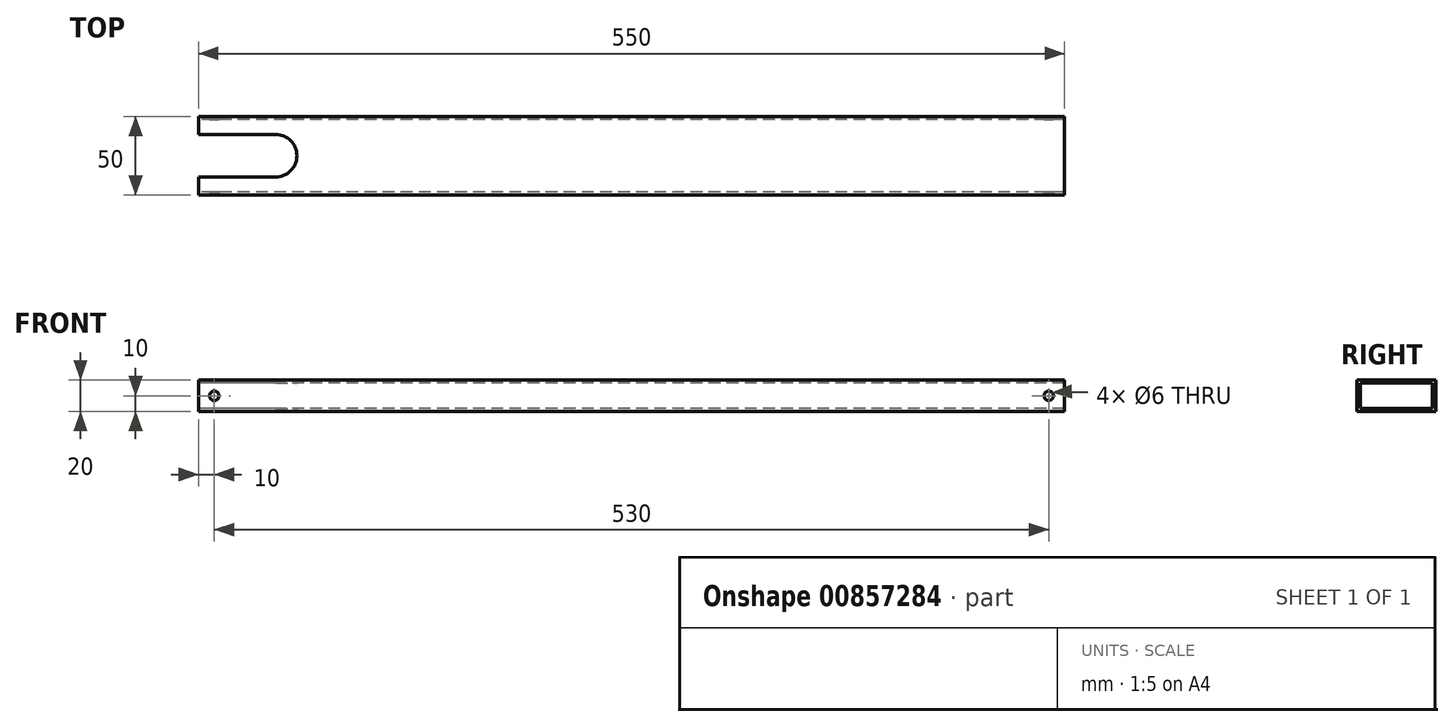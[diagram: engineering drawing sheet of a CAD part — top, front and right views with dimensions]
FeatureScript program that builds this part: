
annotation { "Feature Type Name" : "Feature", "Feature Type Description" : "" }
export const myFeature = defineFeature(function(context is Context, id is Id, definition is map)
    precondition{}
    {
        {
            var Q0;
            Q0=qCreatedBy(makeId("Right.planeOp"),FACE);
            var sketch = newSketch(context, id + "F0", { "sketchPlane" : qUnion([Q0])});
            skLineSegment(sketch, "E0.bottom", {"start": v(0, 0) * mm, "end": v(50, 0) * mm});
            skLineSegment(sketch, "E0.top", {"start": v(0, 20) * mm, "end": v(50, 20) * mm});
            skLineSegment(sketch, "E0.left", {"start": v(0, 0) * mm, "end": v(0, 20) * mm});
            skLineSegment(sketch, "E0.right", {"start": v(50, 0) * mm, "end": v(50, 20) * mm});
            skLineSegment(sketch, "E1.0", {"start": v(2, 18) * mm, "end": v(48, 18) * mm});
            skLineSegment(sketch, "E1.1", {"start": v(2, 2) * mm, "end": v(2, 18) * mm});
            skLineSegment(sketch, "E1.2", {"start": v(2, 2) * mm, "end": v(48, 2) * mm});
            skLineSegment(sketch, "E1.3", {"start": v(48, 2) * mm, "end": v(48, 18) * mm});
            skSolve(sketch);
        }
        {
            var Q0;
            Q0=makeQuery(id+"F0.imprint","IMPRINT",FACE,{"disambiguationData":[TD([[makeQuery(id+"F0.imprint","IMPRINT",EDGE,{"derivedFrom":sQuery(id+"F0.wireOp",EDGE,"E0.bottom")}),1.0]])]});
            extrude(context, id + "F1", {"entities" : qUnion([Q0]), "depth" : 550 * mm, "offsetDistance" : 25.4 * mm});
        }
        {
            var Q0;
            Q0=makeQuery(id+"F1.opExtrude","SWEPT_FACE",FACE,{"disambiguationData":[OSD([sQuery(id+"F0.wireOp",EDGE,"E0.left")])]});
            var sketch = newSketch(context, id + "F2", { "sketchPlane" : qUnion([Q0])});
            skCircle(sketch, "E2", {"center": v(10, 10) * mm, "radius": 3 * mm});
            skCircle(sketch, "E3", {"center": v(540, 10) * mm, "radius": 3 * mm});
            skPoint(sketch, "E3.centerSnap0", {"position": v(550, 10) * mm});
            skLineSegment(sketch, "E4", {"start": v(0, 10) * mm, "end": v(550, 10) * mm, "construction": true});
            skSolve(sketch);
        }
        {
            var Q0;
            Q0 = qSketchRegion(id + "F2", true);
            extrude(context, id + "F3", {"entities" : qUnion([Q0]), "operationType" : NewBodyOperationType.REMOVE, "endBound" : BoundingType.THROUGH_ALL, "oppositeDirection" : true, "depth" : 25.4 * mm, "offsetDistance" : 25.4 * mm});
        }
        {
            var Q0;
            Q0=makeQuery(id+"F1.opExtrude","SWEPT_FACE",FACE,{"disambiguationData":[OSD([sQuery(id+"F0.wireOp",EDGE,"E0.top")])]});
            var sketch = newSketch(context, id + "F4", { "sketchPlane" : qUnion([Q0])});
            skLineSegment(sketch, "E5", {"start": v(10, 0) * mm, "end": v(10, 50) * mm, "construction": true});
            skArc(sketch, "E6", {"start": v(49, 11.5) * mm, "mid": v(62.5, 25) * mm, "end": v(49, 38.5) * mm});
            skLineSegment(sketch, "E7", {"start": v(0, 25) * mm, "end": v(125, 25) * mm, "construction": true});
            skLineSegment(sketch, "E8", {"start": v(49, 38.5) * mm, "end": v(0, 38.5) * mm});
            skLineSegment(sketch, "E9", {"start": v(49, 11.5) * mm, "end": v(0, 11.5) * mm});
            skLineSegment(sketch, "E10", {"start": v(0, 11.5) * mm, "end": v(0, 38.5) * mm});
            skPoint(sketch, "E11", {"position": v(62.5, 25) * mm});
            skSolve(sketch);
        }
        {
            var Q0;
            Q0 = qSketchRegion(id + "F4", true);
            extrude(context, id + "F5", {"entities" : qUnion([Q0]), "operationType" : NewBodyOperationType.REMOVE, "endBound" : BoundingType.THROUGH_ALL, "oppositeDirection" : true, "depth" : 25.4 * mm, "offsetDistance" : 25.4 * mm});
        }
        {
            var Q0;
            Q0=makeQuery(id+"F1.opExtrude","CAP_FACE",FACE,{"disambiguationData":[OSD([sQuery(id+"F0.wireOp",EDGE,"E0.bottom"),sQuery(id+"F0.wireOp",EDGE,"E0.top"),sQuery(id+"F0.wireOp",EDGE,"E0.left"),sQuery(id+"F0.wireOp",EDGE,"E0.right"),sQuery(id+"F0.wireOp",EDGE,"E1.0"),sQuery(id+"F0.wireOp",EDGE,"E1.1"),sQuery(id+"F0.wireOp",EDGE,"E1.2"),sQuery(id+"F0.wireOp",EDGE,"E1.3")])],"isStart":false});
            var Q1;
            {var subQ0=sQuery(id+"F0.wireOp",EDGE,"E1.0");var subQ1=sQuery(id+"F0.wireOp",EDGE,"E0.left");var subQ2=sQuery(id+"F0.wireOp",EDGE,"E0.top");var subQ3=sQuery(id+"F0.wireOp",EDGE,"E0.bottom");var subQ4=sQuery(id+"F0.wireOp",EDGE,"E1.1");var subQ5=sQuery(id+"F0.wireOp",EDGE,"E1.2");Q1=makeQuery(id+"F5.boolean.opBoolean","SPLIT",FACE,{"disambiguationData":[TD([makeQuery(id+"F1.opExtrude","SWEPT_FACE",FACE,{"disambiguationData":[OSD([subQ1])]})])],"derivedFrom":makeQuery(id+"F1.opExtrude","CAP_FACE",FACE,{"disambiguationData":[OSD([subQ3,subQ2,subQ1,sQuery(id+"F0.wireOp",EDGE,"E0.right"),subQ0,subQ4,subQ5,sQuery(id+"F0.wireOp",EDGE,"E1.3")])],"isStart":true})});}
            cPlane(context, id + "F6", {"entities" : qUnion([Q0, Q1]), "cplaneType" : CPlaneType.MID_PLANE, "offset" : 25.4 * mm, "width" : 152.4 * mm, "height" : 152.4 * mm});
        }
    });
